# Revit family: Bath-Drop_In-Whirlpool-Heater-KOHLER-Sunward-K-1162_1
name_source: partatom
category: Plumbing Fixtures
units: mm (PartAtom-declared; Revit-internal decimal feet)

## family parameters
Cut with Voids When Loaded = No
Host = Face
OmniClass Number = 23.31.15.00
OmniClass Title = Bathtubs
Part Type = Normal
Room Calculation Point = No
Round Connector Dimension = Use Diameter
Shared = No

## types (4) — shared parameters
ADA Compliant = No
Amplifer Electrical Connector = Amplifer Electrical Connector
Apparent Load = 1800 VA
Assembly Code = D2010500
Blower Electrical Connector = Blower Electrical Connector
CW Connection = No
Cold Water Inlet = Cold Water Inlet
Date Modified = 08/04/2022
Default Elevation = 0"
Drain Included = No
Electrical Connector = Yes
Electrical Note = Two Dedicated Circuits Required
HW Connection = No
Heater Electrical Connector = Heater Electrical Connector
Height = 21"
Hot Water Inlet = Hot Water Inlet
Length = 60"
Manufacturer = Kohler Co.
Master Format 2014 = 22 41 19
Master Format 2014 Name = Residential Bathtubs
Material = Acrylic
Product Documentation Link = https://www.us.kohler.com
Product Name = Sunward
Product Page URL = http://www.us.kohler.com
Pump Electrical Connector = Pump Electrical Connector
URL = https://www.us.kohler.com
Vent Connection = No
Voltage = 120 V
Waste Connection = Yes
Waste Water Outlet = Waste Water Outlet
WaterSense Certified = No
Width = 42"

## per-type parameters (varying)
| type | Description | Finish | Model | Type |
| 0-White | 60 Inch x 42 Inch drop-in whirlpool bath with end drain and heater | KOHLER-Acrylic-0-White | K-1162-H-0 | 1 |
| 96-Biscuit | 60 Inch x 42 Inch drop-in whirlpool bath with end drain and heater | KOHLER-Acrylic-96-Biscuit | K-1162-H-96 | 2 |
| Custom Pump Location, 0-White | 60 Inch x 42 Inch drop-in whirlpool bath with end drain, heater and custom pump location | KOHLER-Acrylic-0-White | K-1162-HB-0 | 3 |
| Custom Pump Location, 96-Biscuit | 60 Inch x 42 Inch drop-in whirlpool bath with end drain, heater and custom pump location | KOHLER-Acrylic-96-Biscuit | K-1162-HB-96 | 4 |

## geometry (parser evidence)
native form markers: Sweep x5
no freeform markers — native parametric forms only
